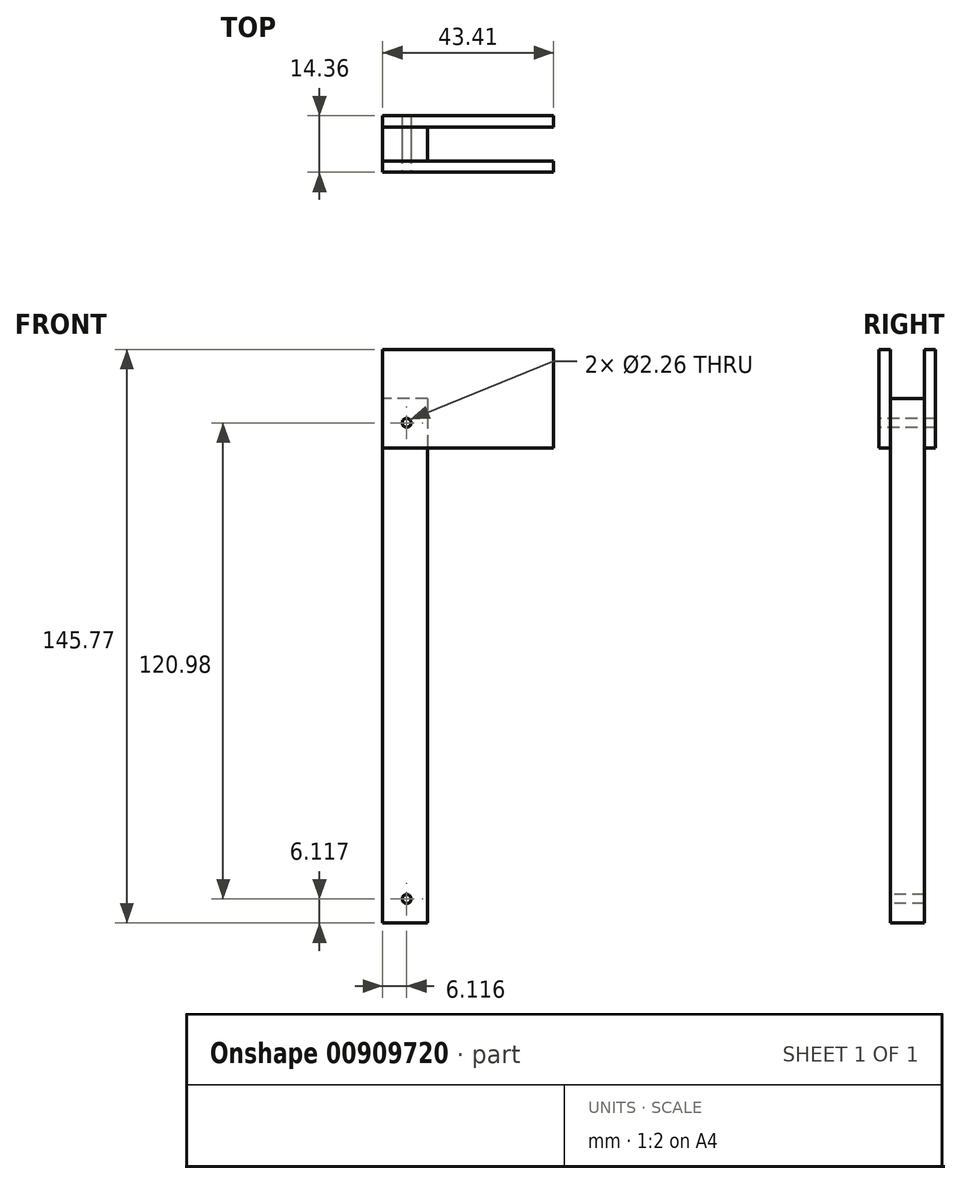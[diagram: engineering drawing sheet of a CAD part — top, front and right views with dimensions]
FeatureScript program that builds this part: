
annotation { "Feature Type Name" : "Feature", "Feature Type Description" : "" }
export const myFeature = defineFeature(function(context is Context, id is Id, definition is map)
    precondition{}
    {
        {
            var Q0;
            Q0=qCreatedBy(makeId("Front.planeOp"),FACE);
            var sketch = newSketch(context, id + "F0", { "sketchPlane" : qUnion([Q0])});
            skLineSegment(sketch, "E0.bottom", {"start": v(5.72, 66.62) * mm, "end": v(-5.72, 66.62) * mm});
            skLineSegment(sketch, "E0.top", {"start": v(5.72, -66.62) * mm, "end": v(-5.71, -66.62) * mm});
            skLineSegment(sketch, "E0.left", {"start": v(5.71, 66.62) * mm, "end": v(5.72, -66.62) * mm});
            skLineSegment(sketch, "E0.right", {"start": v(-5.72, 66.62) * mm, "end": v(-5.71, -66.62) * mm});
            skPoint(sketch, "E0.middle", {"position": v(0, 0) * mm});
            skSolve(sketch);
        }
        {
            var Q0;
            Q0=makeQuery(id+"F0.imprint","IMPRINT",FACE,{"disambiguationData":[TD([[makeQuery(id+"F0.imprint","IMPRINT",EDGE,{"derivedFrom":sQuery(id+"F0.wireOp",EDGE,"E0.bottom")}),1.0]])]});
            extrude(context, id + "F1", {"entities" : qUnion([Q0]), "endBound" : BoundingType.SYMMETRIC, "depth" : 8.6 * mm, "offsetDistance" : 25.4 * mm});
        }
        {
            var Q0;
            Q0=makeQuery(id+"F1.opExtrude","CAP_FACE",FACE,{"disambiguationData":[OSD([sQuery(id+"F0.wireOp",EDGE,"E0.bottom"),sQuery(id+"F0.wireOp",EDGE,"E0.top"),sQuery(id+"F0.wireOp",EDGE,"E0.left"),sQuery(id+"F0.wireOp",EDGE,"E0.right")])],"isStart":false});
            var sketch = newSketch(context, id + "F2", { "sketchPlane" : qUnion([Q0])});
            skLineSegment(sketch, "E1", {"start": v(0, 66.62) * mm, "end": v(0, 54.05) * mm, "construction": true});
            skLineSegment(sketch, "E2", {"start": v(0, 54.05) * mm, "end": v(-5.72, 54.05) * mm, "construction": true});
            skLineSegment(sketch, "E3", {"start": v(5.72, 66.62) * mm, "end": v(5.72, 79.15) * mm, "construction": true});
            skLineSegment(sketch, "E4.bottom", {"start": v(-5.72, 54.05) * mm, "end": v(5.72, 54.05) * mm});
            skLineSegment(sketch, "E4.top", {"start": v(-5.72, 79.15) * mm, "end": v(5.72, 79.15) * mm});
            skLineSegment(sketch, "E4.left", {"start": v(-5.72, 54.05) * mm, "end": v(-5.72, 79.15) * mm});
            skLineSegment(sketch, "E5", {"start": v(5.72, 54.05) * mm, "end": v(37.7, 54.05) * mm, "construction": true});
            skLineSegment(sketch, "E6.bottom", {"start": v(5.72, 79.15) * mm, "end": v(37.7, 79.15) * mm});
            skLineSegment(sketch, "E6.top", {"start": v(5.72, 54.05) * mm, "end": v(37.7, 54.05) * mm});
            skLineSegment(sketch, "E6.left", {"start": v(5.72, 79.15) * mm, "end": v(5.72, 54.05) * mm, "construction": true});
            skLineSegment(sketch, "E6.right", {"start": v(37.7, 79.15) * mm, "end": v(37.7, 54.05) * mm});
            skSolve(sketch);
        }
        {
            var Q0;
            {var subQ3=sQuery(id+"F2.wireOp",EDGE,"E4.top");Q0=makeQuery(id+"F2.imprint","IMPRINT",FACE,{"disambiguationData":[TD([[makeQuery(id+"F2.imprint","IMPRINT",EDGE,{"derivedFrom":subQ3}),-1.0]])]});}
            var Q1;
            {var subQ0=sQuery(id+"F2.wireOp",EDGE,"E4.bottom");Q1=makeQuery(id+"F2.imprint","IMPRINT",FACE,{"disambiguationData":[TD([[makeQuery(id+"F2.imprint","IMPRINT",EDGE,{"derivedFrom":subQ0}),1.0]])]});}
            extrude(context, id + "F3", {"entities" : qUnion([Q0, Q1]), "depth" : 2.87 * mm, "offsetDistance" : 25.4 * mm});
        }
        {
            var Q0;
            Q0=makeQuery(id+"F3.opExtrude","SWEPT_BODY",BODY,{"disambiguationData":[OSD([sQuery(id+"F2.wireOp",EDGE,"E4.bottom"),sQuery(id+"F2.wireOp",EDGE,"E4.top"),sQuery(id+"F2.wireOp",EDGE,"E4.left"),sQuery(id+"F2.wireOp",EDGE,"E6.bottom"),sQuery(id+"F2.wireOp",EDGE,"E6.top"),sQuery(id+"F2.wireOp",EDGE,"E6.right")])]});
            var Q1;
            Q1=qCreatedBy(makeId("Front.planeOp"),FACE);
            mirror(context, id + "F4", {"operationType" : NewBodyOperationType.ADD, "entities" : qUnion([Q0]), "mirrorPlane" : qUnion([Q1])});
        }
        {
            var Q0;
            Q0=makeQuery(id+"F1.opExtrude","CAP_FACE",FACE,{"disambiguationData":[OSD([sQuery(id+"F0.wireOp",EDGE,"E0.bottom"),sQuery(id+"F0.wireOp",EDGE,"E0.top"),sQuery(id+"F0.wireOp",EDGE,"E0.left"),sQuery(id+"F0.wireOp",EDGE,"E0.right")])],"isStart":false});
            var sketch = newSketch(context, id + "F5", { "sketchPlane" : qUnion([Q0])});
            skLineSegment(sketch, "E7", {"start": v(-5.71, -60.5) * mm, "end": v(0.4, -60.5) * mm});
            skLineSegment(sketch, "E8", {"start": v(0.4, -60.5) * mm, "end": v(0.4, -66.62) * mm});
            skLineSegment(sketch, "E9.MirrorCS", {"start": v(-5.71, 60.5) * mm, "end": v(0.4, 60.5) * mm});
            skLineSegment(sketch, "E10.MirrorCS", {"start": v(0.4, 60.5) * mm, "end": v(0.4, 66.62) * mm});
            skPoint(sketch, "E11", {"position": v(0.4, -60.5) * mm});
            skPoint(sketch, "E12", {"position": v(0.4, 60.5) * mm});
            skSolve(sketch);
        }
        {
            var Q0;
            Q0=makeQuery(id+"F3.opExtrude","CAP_FACE",FACE,{"disambiguationData":[OSD([sQuery(id+"F2.wireOp",EDGE,"E4.bottom"),sQuery(id+"F2.wireOp",EDGE,"E4.top"),sQuery(id+"F2.wireOp",EDGE,"E4.left"),sQuery(id+"F2.wireOp",EDGE,"E6.bottom"),sQuery(id+"F2.wireOp",EDGE,"E6.top"),sQuery(id+"F2.wireOp",EDGE,"E6.right")])],"isStart":false});
            var sketch = newSketch(context, id + "F6", { "sketchPlane" : qUnion([Q0])});
            skLineSegment(sketch, "E13", {"start": v(-5.72, 66.6) * mm, "end": v(0.4, 66.6) * mm});
            skLineSegment(sketch, "E14", {"start": v(0.4, 66.6) * mm, "end": v(0.4, 60.48) * mm});
            skPoint(sketch, "E15", {"position": v(0.4, 60.48) * mm});
            skSolve(sketch);
        }
        {
            var Q0;
            Q0=sQuery(id+"F6.wireOp",VERTEX,"E15");
            var Q1;
            Q1=makeQuery(id+"F1.opExtrude","SWEPT_BODY",BODY,{"disambiguationData":[OSD([sQuery(id+"F0.wireOp",EDGE,"E0.bottom"),sQuery(id+"F0.wireOp",EDGE,"E0.top"),sQuery(id+"F0.wireOp",EDGE,"E0.left"),sQuery(id+"F0.wireOp",EDGE,"E0.right")])]});
            hole(context, id + "F7", {"style" : HoleStyle.SIMPLE, "endStyle" : HoleEndStyle.THROUGH, "standardTappedOrClearance" : lookupTablePath({ "standard" : "ANSI", "engagement" : "75%", "pitch" : "40 tpi", "size" : "#4", "type" : "Tapped" }), "standardBlindInLast" : lookupTablePath({ "standard" : "ANSI", "engagement" : "75%", "pitch" : "40 tpi", "size" : "#4", "type" : "Tapped" }), "holeDiameter" : 2.26 * mm, "majorDiameter" : 2.84 * mm, "showTappedDepth" : true, "isTappedThrough" : true, "tappedDepth" : 12.7 * mm, "tapClearance" : 3, "locations" : qUnion([Q0]), "scope" : qUnion([Q1])});
        }
        {
            var Q0;
            Q0=sQuery(id+"F5.wireOp",VERTEX,"E11");
            var Q1;
            Q1=makeQuery(id+"F1.opExtrude","SWEPT_BODY",BODY,{"disambiguationData":[OSD([sQuery(id+"F0.wireOp",EDGE,"E0.bottom"),sQuery(id+"F0.wireOp",EDGE,"E0.top"),sQuery(id+"F0.wireOp",EDGE,"E0.left"),sQuery(id+"F0.wireOp",EDGE,"E0.right")])]});
            hole(context, id + "F8", {"style" : HoleStyle.SIMPLE, "endStyle" : HoleEndStyle.THROUGH, "standardTappedOrClearance" : lookupTablePath({ "standard" : "ANSI", "engagement" : "75%", "pitch" : "40 tpi", "size" : "#4", "type" : "Tapped" }), "standardBlindInLast" : lookupTablePath({ "standard" : "ANSI", "engagement" : "75%", "pitch" : "40 tpi", "size" : "#4", "type" : "Tapped" }), "holeDiameter" : 2.26 * mm, "majorDiameter" : 2.84 * mm, "showTappedDepth" : true, "isTappedThrough" : true, "tappedDepth" : 12.7 * mm, "tapClearance" : 3, "locations" : qUnion([Q0]), "scope" : qUnion([Q1])});
        }
    });
